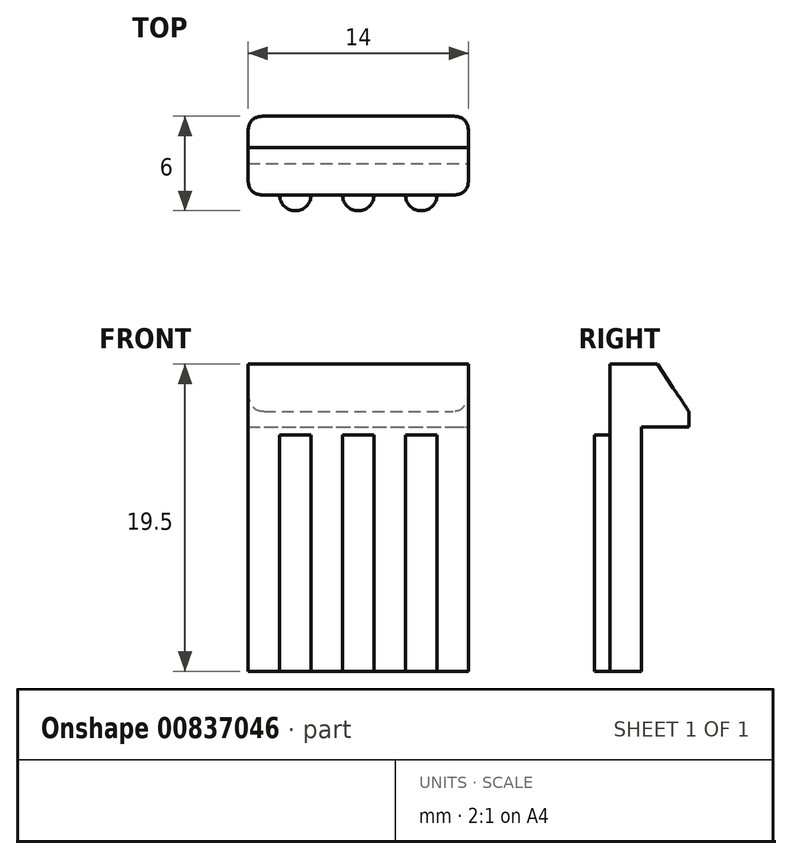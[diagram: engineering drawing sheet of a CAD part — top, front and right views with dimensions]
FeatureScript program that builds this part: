
annotation { "Feature Type Name" : "Feature", "Feature Type Description" : "" }
export const myFeature = defineFeature(function(context is Context, id is Id, definition is map)
    precondition{}
    {
        {
            var Q0;
            Q0=qCreatedBy(makeId("Top.planeOp"),FACE);
            var sketch = newSketch(context, id + "F0", { "sketchPlane" : qUnion([Q0])});
            skLineSegment(sketch, "E0.bottom", {"start": v(-7, 1) * mm, "end": v(7, 1) * mm});
            skLineSegment(sketch, "E0.top", {"start": v(-7, -1) * mm, "end": v(7, -1) * mm});
            skLineSegment(sketch, "E0.left", {"start": v(-7, 1) * mm, "end": v(-7, -1) * mm});
            skLineSegment(sketch, "E0.right", {"start": v(7, 1) * mm, "end": v(7, -1) * mm});
            skPoint(sketch, "E0.middle", {"position": v(0, 0) * mm});
            skSolve(sketch);
        }
        {
            var Q0;
            {var subQ0=sQuery(id+"F0.wireOp",EDGE,"E0.bottom");Q0=makeQuery(id+"F0.imprint","IMPRINT",FACE,{"disambiguationData":[TD([[makeQuery(id+"F0.imprint","IMPRINT",EDGE,{"derivedFrom":subQ0}),-1.0]])]});}
            extrude(context, id + "F1", {"entities" : qUnion([Q0]), "depth" : 15.5 * mm, "offsetDistance" : 25 * mm});
        }
        {
            var Q0;
            Q0=makeQuery(id+"F1.opExtrude","CAP_FACE",FACE,{"disambiguationData":[OSD([sQuery(id+"F0.wireOp",EDGE,"E0.bottom"),sQuery(id+"F0.wireOp",EDGE,"E0.left"),sQuery(id+"F0.wireOp",EDGE,"E0.right"),sQuery(id+"F0.wireOp",EDGE,"E0.top")])],"isStart":false});
            var sketch = newSketch(context, id + "F2", { "sketchPlane" : qUnion([Q0])});
            skLineSegment(sketch, "E1.bottom", {"start": v(-7, -1) * mm, "end": v(7, -1) * mm});
            skLineSegment(sketch, "E1.top", {"start": v(-7, 4) * mm, "end": v(7, 4) * mm});
            skLineSegment(sketch, "E1.left", {"start": v(-7, -1) * mm, "end": v(-7, 4) * mm});
            skLineSegment(sketch, "E1.right", {"start": v(7, -1) * mm, "end": v(7, 4) * mm});
            skSolve(sketch);
        }
        {
            var Q0;
            {var subQ0=sQuery(id+"F2.wireOp",EDGE,"E1.top");Q0=makeQuery(id+"F2.imprint","IMPRINT",FACE,{"disambiguationData":[TD([[makeQuery(id+"F2.imprint","IMPRINT",EDGE,{"derivedFrom":subQ0}),-1.0]])]});}
            var Q1;
            {var subQ0=sQuery(id+"F2.wireOp",EDGE,"E1.bottom");Q1=makeQuery(id+"F2.imprint","IMPRINT",FACE,{"disambiguationData":[TD([[makeQuery(id+"F2.imprint","IMPRINT",EDGE,{"derivedFrom":subQ0}),1.0]])]});}
            extrude(context, id + "F3", {"entities" : qUnion([Q0, Q1]), "operationType" : NewBodyOperationType.ADD, "depth" : 4 * mm, "offsetDistance" : 25 * mm});
        }
        {
            var Q0;
            Q0=makeQuery(id+"F3.opExtrude","CAP_EDGE",EDGE,{"disambiguationData":[OSD([sQuery(id+"F2.wireOp",EDGE,"E1.top")])],"isStart":false});
            chamfer(context, id + "F4", {"entities" : qUnion([Q0]), "chamferType" : ChamferType.TWO_OFFSETS, "width1" : 3 * mm, "oppositeDirection" : false, "width2" : 2 * mm, "tangentPropagation" : true});
        }
        {
            var Q0;
            Q0=makeQuery(id+"F3.boolean.opBoolean","MERGE",EDGE,{"derivedFrom":[makeQuery(id+"F1.opExtrude","SWEPT_EDGE",EDGE,{"disambiguationData":[OSD([sQuery(id+"F0.wireOp",EDGE,"E0.left"),sQuery(id+"F0.wireOp",EDGE,"E0.top")])]}),makeQuery(id+"F3.opExtrude","SWEPT_EDGE",EDGE,{"disambiguationData":[OSD([sQuery(id+"F2.wireOp",EDGE,"E1.bottom"),sQuery(id+"F2.wireOp",EDGE,"E1.left")])]})]});
            var Q1;
            Q1=makeQuery(id+"F3.boolean.opBoolean","MERGE",EDGE,{"derivedFrom":[makeQuery(id+"F1.opExtrude","SWEPT_EDGE",EDGE,{"disambiguationData":[OSD([sQuery(id+"F0.wireOp",EDGE,"E0.right"),sQuery(id+"F0.wireOp",EDGE,"E0.top")])]}),makeQuery(id+"F3.opExtrude","SWEPT_EDGE",EDGE,{"disambiguationData":[OSD([sQuery(id+"F2.wireOp",EDGE,"E1.bottom"),sQuery(id+"F2.wireOp",EDGE,"E1.right")])]})]});
            var Q2;
            Q2=makeQuery(id+"F3.opExtrude","SWEPT_EDGE",EDGE,{"disambiguationData":[OSD([sQuery(id+"F2.wireOp",EDGE,"E1.top"),sQuery(id+"F2.wireOp",EDGE,"E1.left")])]});
            var Q3;
            Q3=makeQuery(id+"F3.opExtrude","SWEPT_EDGE",EDGE,{"disambiguationData":[OSD([sQuery(id+"F2.wireOp",EDGE,"E1.top"),sQuery(id+"F2.wireOp",EDGE,"E1.right")])]});
            fillet(context, id + "F5", {"entities" : qUnion([Q0, Q1, Q2, Q3]), "radius" : 1 * mm, "rho" : 0.5, "crossSection" : FilletCrossSection.CONIC, "allowEdgeOverflow" : false});
        }
        {
            var Q0;
            Q0=makeQuery(id+"F1.opExtrude","CAP_FACE",FACE,{"disambiguationData":[OSD([sQuery(id+"F0.wireOp",EDGE,"E0.bottom"),sQuery(id+"F0.wireOp",EDGE,"E0.left"),sQuery(id+"F0.wireOp",EDGE,"E0.right"),sQuery(id+"F0.wireOp",EDGE,"E0.top")])],"isStart":true});
            var sketch = newSketch(context, id + "F6", { "sketchPlane" : qUnion([Q0])});
            skCircle(sketch, "E2", {"center": v(0, 1) * mm, "radius": 1 * mm});
            skCircle(sketch, "E3", {"center": v(-4, 1) * mm, "radius": 1 * mm});
            skCircle(sketch, "E4", {"center": v(4, 1) * mm, "radius": 1 * mm});
            skSolve(sketch);
        }
        {
            var Q0;
            {var subQ0=sQuery(id+"F6.wireOp",EDGE,"E2");var subQ1=makeQuery(id+"F1.opExtrude","CAP_EDGE",EDGE,{"disambiguationData":[OSD([sQuery(id+"F0.wireOp",EDGE,"E0.top")])],"isStart":true});var subQ2=makeQuery(id+"F6.imprint","INTERSECT",VERTEX,{"disambiguationData":[OD(0.0)],"derivedFrom":[subQ1,subQ0]});Q0=makeQuery(id+"F6.imprint","IMPRINT",FACE,{"disambiguationData":[TD([[makeQuery(id+"F6.imprint","IMPRINT",EDGE,{"disambiguationData":[TD([[subQ2,1.0]])],"derivedFrom":subQ0}),1.0]])]});}
            var Q1;
            {var subQ0=sQuery(id+"F6.wireOp",EDGE,"E3");var subQ1=makeQuery(id+"F1.opExtrude","CAP_EDGE",EDGE,{"disambiguationData":[OSD([sQuery(id+"F0.wireOp",EDGE,"E0.top")])],"isStart":true});var subQ2=makeQuery(id+"F6.imprint","INTERSECT",VERTEX,{"disambiguationData":[OD(0.0)],"derivedFrom":[subQ1,subQ0]});Q1=makeQuery(id+"F6.imprint","IMPRINT",FACE,{"disambiguationData":[TD([[makeQuery(id+"F6.imprint","IMPRINT",EDGE,{"disambiguationData":[TD([[subQ2,1.0]])],"derivedFrom":subQ0}),1.0]])]});}
            var Q2;
            {var subQ0=sQuery(id+"F6.wireOp",EDGE,"E4");var subQ1=makeQuery(id+"F1.opExtrude","CAP_EDGE",EDGE,{"disambiguationData":[OSD([sQuery(id+"F0.wireOp",EDGE,"E0.top")])],"isStart":true});var subQ2=makeQuery(id+"F6.imprint","INTERSECT",VERTEX,{"disambiguationData":[OD(0.0)],"derivedFrom":[subQ1,subQ0]});Q2=makeQuery(id+"F6.imprint","IMPRINT",FACE,{"disambiguationData":[TD([[makeQuery(id+"F6.imprint","IMPRINT",EDGE,{"disambiguationData":[TD([[subQ2,-1.0]])],"derivedFrom":subQ0}),1.0]])]});}
            extrude(context, id + "F7", {"entities" : qUnion([Q0, Q1, Q2]), "operationType" : NewBodyOperationType.ADD, "oppositeDirection" : true, "depth" : 15 * mm, "offsetDistance" : 25 * mm});
        }
    });
